# Revit family: PRD_FrankeWS_EyeWshFntns_EyeShower_FAID108
name_source: partatom
category: Plumbing Fixtures
revit_build: Autodesk Revit 2018 (Build: 20190510_1515(x64)
units: mm (PartAtom-declared; Revit-internal decimal feet)

## family parameters
Cut with Voids When Loaded = Yes
Host = Face
OmniClass Number = 23.45.05.14.24
OmniClass Title = Eye Wash Fountains
Part Type = Normal
Room Calculation Point = No
Round Connector Dimension = Use Diameter
Shared = Yes

## types (1)
- FAID108
    AccessoriesMaterial = PRD_AR_StainlessSteel_SatinFinished
    AssetType = Fixed
    BIMObjectName = PRD_AR_EyeWashingFountains_EyeShower_FAID108
    BasinMaterial = PRD_AR_Plastic_Green
    Category = Pr_40_20_27_28, Eye-wash fountains
    Color = green
    Default Elevation = 925 mm  [stored 3.03478 ft]
    Description = Eye-wash and face-wash fountain with water collection basin made of green plastic with bracket for wall mounting. Hand shower with hose connection, Meets the requirements of EN 15154-2 and ANSI Z358.1-2014, green plastic housing, dust protection cap with user instructions. Mounting material included.
    DiameterNominal = 15  [stored 0.0492126 ft]
    DrainSize = 15 mm  [stored 0.0492126 ft]
    DripPan = Yes
    DurationUnit = year
    Features = hand shower with hose connection
    FittingMaterial = PRD_AR_Plastic_White
    GrossWeight = 6.68 kg
    HandShowerMaterial = PRD_AR_Plastic_Green
    HasTray = TRUE
    IfcExportAs = IfcSanitaryTerminalType
    IfcExportType = SHOWER
    InletSize = DN 15
    IntegralAccessories = mounting material included
    Manufacturer = KWC Group AG
    ManufacturerName = KWC Group AG
    ManufacturerURL = www.kwc.com
    Material = plastic
    Model = FAID108
    ModelNumber = 2000101103
    ModelReference = FAID108
    NBSDescription = Wash fountain packages
    NBSReference = 45-35-70/406
    Name = Eye Shower FAID108
    NetWeight = 5.80 kg
    NominalDepth = 460 mm  [stored 1.50919 ft]
    NominalHeight = 390 mm  [stored 1.27953 ft]
    NominalWidth = 400 mm  [stored 1.31234 ft]
    ProductInformation = https://pim.kwc.com
    ShowerType = Individual
    Size = 400 x 390 x 460 mm (W x H x D)
    TypeOfFitting = Wall installation
    TypeOfOperation = Trigger button
    URL = www.kwc.com
    Uniclass2015Code = Pr_40_20_27_28
    Uniclass2015Title = Eye-wash fountains
    Uniclass2015Version = Products v1.17
    Version = 1
    WarrantyDurationUnit = year

note: [stored X ft] marks values corroborated as IEEE doubles in the binary element streams (Revit-internal decimal feet)

## geometry (parser evidence)
native form markers: Sweep x3
no freeform markers — native parametric forms only
